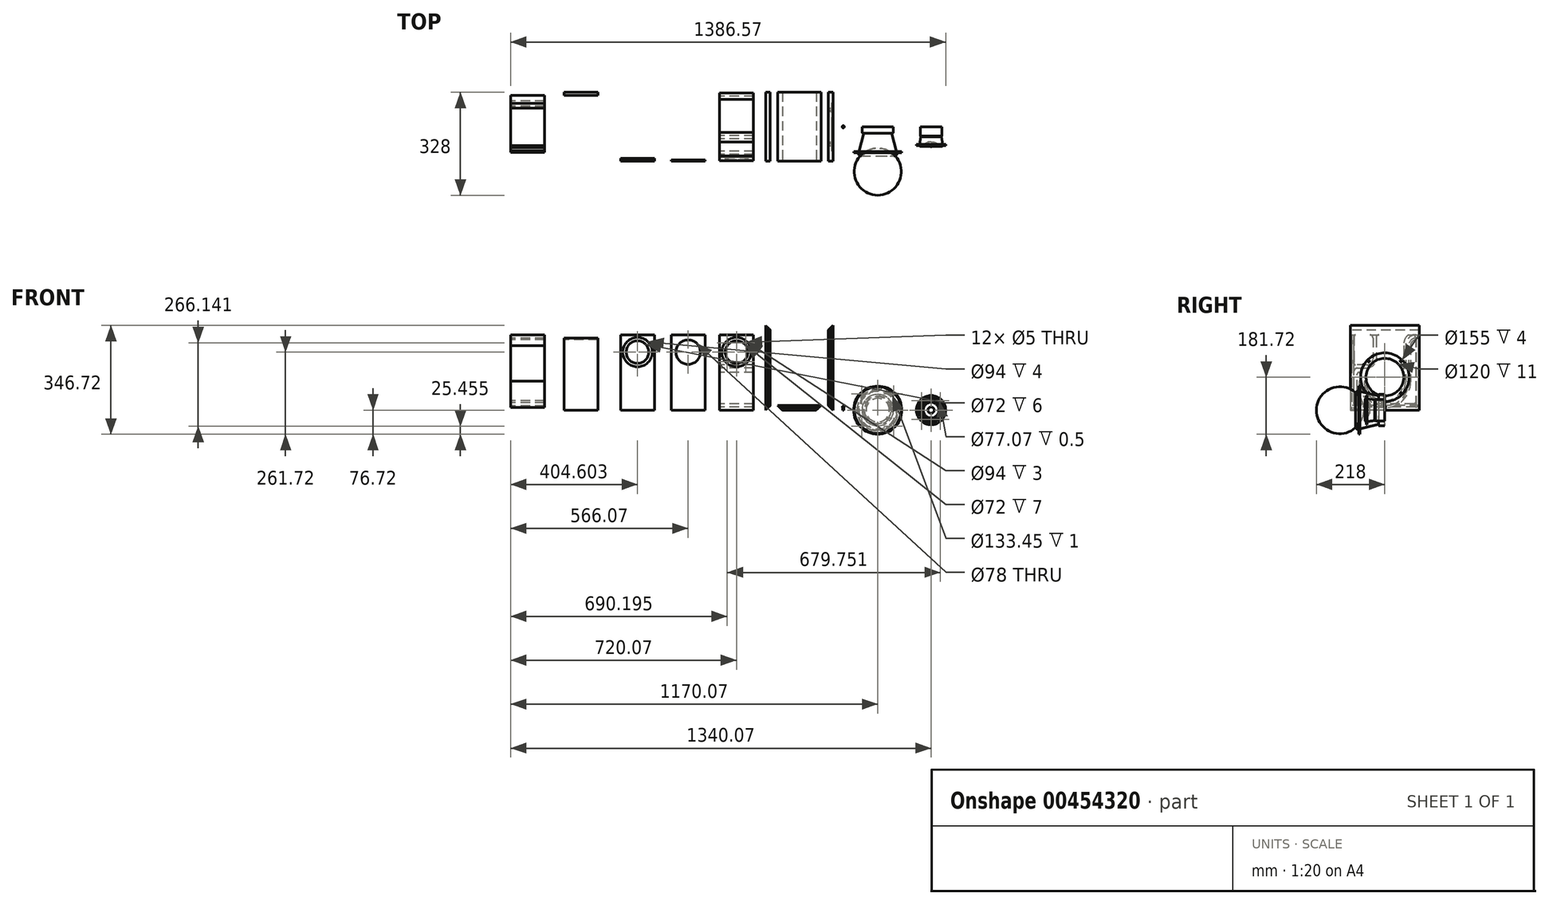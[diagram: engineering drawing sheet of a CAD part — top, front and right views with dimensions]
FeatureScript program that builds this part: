
annotation { "Feature Type Name" : "Feature", "Feature Type Description" : "" }
export const myFeature = defineFeature(function(context is Context, id is Id, definition is map)
    precondition{}
    {
        {
            var Q0;
            Q0=qCreatedBy(makeId("Top.planeOp"),FACE);
            var sketch = newSketch(context, id + "F0", { "sketchPlane" : qUnion([Q0])});
            skLineSegment(sketch, "E0", {"start": v(0, 207.9) * mm, "end": v(0, 427.9) * mm});
            skLineSegment(sketch, "E1", {"start": v(0, 427.9) * mm, "end": v(108, 427.9) * mm});
            skSolve(sketch);
        }
        {
            var Q0;
            Q0=qCreatedBy(makeId("Top.planeOp"),FACE);
            var sketch = newSketch(context, id + "F1", { "sketchPlane" : qUnion([Q0])});
            skLineSegment(sketch, "E2.bottom", {"start": v(-69, -110) * mm, "end": v(69, -110) * mm});
            skLineSegment(sketch, "E2.top", {"start": v(-69, 110) * mm, "end": v(69, 110) * mm});
            skLineSegment(sketch, "E2.left", {"start": v(-69, -110) * mm, "end": v(-69, 110) * mm});
            skLineSegment(sketch, "E2.right", {"start": v(69, -110) * mm, "end": v(69, 110) * mm});
            skPoint(sketch, "E2.middle", {"position": v(0, 0) * mm});
            skSolve(sketch);
        }
        {
            var Q0;
            Q0 = qSketchRegion(id + "F1", true);
            extrude(context, id + "F2", {"entities" : qUnion([Q0]), "depth" : 15 * mm});
        }
        {
            var Q0;
            Q0=makeQuery(id+"F2.opExtrude","SWEPT_FACE",FACE,{"disambiguationData":[OSD([sQuery(id+"F1.wireOp",EDGE,"E2.bottom")])]});
            var sketch = newSketch(context, id + "F3", { "sketchPlane" : qUnion([Q0])});
            skLineSegment(sketch, "E3.bottom", {"start": v(-69, 1) * mm, "end": v(69, 1) * mm});
            skLineSegment(sketch, "E3.top", {"start": v(-69, 2) * mm, "end": v(69, 2) * mm});
            skLineSegment(sketch, "E3.left", {"start": v(-69, 1) * mm, "end": v(-69, 2) * mm});
            skLineSegment(sketch, "E3.right", {"start": v(69, 1) * mm, "end": v(69, 2) * mm});
            skLineSegment(sketch, "E4.0.1.0", {"start": v(-69, 4) * mm, "end": v(69, 4) * mm});
            skLineSegment(sketch, "E4.0.1.1", {"start": v(-69, 3) * mm, "end": v(-69, 4) * mm});
            skLineSegment(sketch, "E4.0.1.2", {"start": v(-69, 3) * mm, "end": v(69, 3) * mm});
            skLineSegment(sketch, "E4.0.1.3", {"start": v(69, 3) * mm, "end": v(69, 4) * mm});
            skLineSegment(sketch, "E4.0.2.0", {"start": v(-69, 6) * mm, "end": v(69, 6) * mm});
            skLineSegment(sketch, "E4.0.2.1", {"start": v(-69, 5) * mm, "end": v(-69, 6) * mm});
            skLineSegment(sketch, "E4.0.2.2", {"start": v(-69, 5) * mm, "end": v(69, 5) * mm});
            skLineSegment(sketch, "E4.0.2.3", {"start": v(69, 5) * mm, "end": v(69, 6) * mm});
            skLineSegment(sketch, "E4.0.3.0", {"start": v(-69, 8) * mm, "end": v(69, 8) * mm});
            skLineSegment(sketch, "E4.0.3.1", {"start": v(-69, 7) * mm, "end": v(-69, 8) * mm});
            skLineSegment(sketch, "E4.0.3.2", {"start": v(-69, 7) * mm, "end": v(69, 7) * mm});
            skLineSegment(sketch, "E4.0.3.3", {"start": v(69, 7) * mm, "end": v(69, 8) * mm});
            skLineSegment(sketch, "E4.0.4.0", {"start": v(-69, 10) * mm, "end": v(69, 10) * mm});
            skLineSegment(sketch, "E4.0.4.1", {"start": v(-69, 9) * mm, "end": v(-69, 10) * mm});
            skLineSegment(sketch, "E4.0.4.2", {"start": v(-69, 9) * mm, "end": v(69, 9) * mm});
            skLineSegment(sketch, "E4.0.4.3", {"start": v(69, 9) * mm, "end": v(69, 10) * mm});
            skLineSegment(sketch, "E4.direction1", {"start": v(-69, 2) * mm, "end": v(-45, 2) * mm, "construction": true});
            skLineSegment(sketch, "E4.direction2", {"start": v(-69, 2) * mm, "end": v(-69, 4) * mm, "construction": true});
            skLineSegment(sketch, "E5.0.0.5", {"start": v(-69, 12) * mm, "end": v(69, 12) * mm});
            skLineSegment(sketch, "E5.3.0.5", {"start": v(-69, 11) * mm, "end": v(-69, 12) * mm});
            skLineSegment(sketch, "E5.6.0.5", {"start": v(-69, 11) * mm, "end": v(69, 11) * mm});
            skLineSegment(sketch, "E5.9.0.5", {"start": v(69, 11) * mm, "end": v(69, 12) * mm});
            skLineSegment(sketch, "E5.0.0.6", {"start": v(-69, 14) * mm, "end": v(69, 14) * mm});
            skLineSegment(sketch, "E5.3.0.6", {"start": v(-69, 13) * mm, "end": v(-69, 14) * mm});
            skLineSegment(sketch, "E5.6.0.6", {"start": v(-69, 13) * mm, "end": v(69, 13) * mm});
            skLineSegment(sketch, "E5.9.0.6", {"start": v(69, 13) * mm, "end": v(69, 14) * mm});
            skSolve(sketch);
        }
        {
            var Q0;
            Q0 = qSketchRegion(id + "F3", true);
            extrude(context, id + "F4", {"entities" : qUnion([Q0]), "operationType" : NewBodyOperationType.REMOVE, "oppositeDirection" : true, "depth" : 0.1 * mm});
        }
        {
            var Q0;
            Q0=makeQuery(id+"F2.opExtrude","SWEPT_FACE",FACE,{"disambiguationData":[OSD([sQuery(id+"F1.wireOp",EDGE,"E2.top")])]});
            var sketch = newSketch(context, id + "F5", { "sketchPlane" : qUnion([Q0])});
            skLineSegment(sketch, "E6.bottom", {"start": v(-75, 1) * mm, "end": v(75, 1) * mm});
            skLineSegment(sketch, "E6.top", {"start": v(-75, 2) * mm, "end": v(75, 2) * mm});
            skLineSegment(sketch, "E6.left", {"start": v(-75, 1) * mm, "end": v(-75, 2) * mm});
            skLineSegment(sketch, "E6.right", {"start": v(75, 1) * mm, "end": v(75, 2) * mm});
            skLineSegment(sketch, "E7.0.1.0", {"start": v(-75, 4) * mm, "end": v(75, 4) * mm});
            skLineSegment(sketch, "E7.0.1.1", {"start": v(-75, 3) * mm, "end": v(-75, 4) * mm});
            skLineSegment(sketch, "E7.0.1.2", {"start": v(-75, 3) * mm, "end": v(75, 3) * mm});
            skLineSegment(sketch, "E7.0.1.3", {"start": v(75, 3) * mm, "end": v(75, 4) * mm});
            skLineSegment(sketch, "E7.0.2.0", {"start": v(-75, 6) * mm, "end": v(75, 6) * mm});
            skLineSegment(sketch, "E7.0.2.1", {"start": v(-75, 5) * mm, "end": v(-75, 6) * mm});
            skLineSegment(sketch, "E7.0.2.2", {"start": v(-75, 5) * mm, "end": v(75, 5) * mm});
            skLineSegment(sketch, "E7.0.2.3", {"start": v(75, 5) * mm, "end": v(75, 6) * mm});
            skLineSegment(sketch, "E7.0.3.0", {"start": v(-75, 8) * mm, "end": v(75, 8) * mm});
            skLineSegment(sketch, "E7.0.3.1", {"start": v(-75, 7) * mm, "end": v(-75, 8) * mm});
            skLineSegment(sketch, "E7.0.3.2", {"start": v(-75, 7) * mm, "end": v(75, 7) * mm});
            skLineSegment(sketch, "E7.0.3.3", {"start": v(75, 7) * mm, "end": v(75, 8) * mm});
            skLineSegment(sketch, "E7.0.4.0", {"start": v(-75, 10) * mm, "end": v(75, 10) * mm});
            skLineSegment(sketch, "E7.0.4.1", {"start": v(-75, 9) * mm, "end": v(-75, 10) * mm});
            skLineSegment(sketch, "E7.0.4.2", {"start": v(-75, 9) * mm, "end": v(75, 9) * mm});
            skLineSegment(sketch, "E7.0.4.3", {"start": v(75, 9) * mm, "end": v(75, 10) * mm});
            skLineSegment(sketch, "E7.direction1", {"start": v(-75, 2) * mm, "end": v(-45, 2) * mm, "construction": true});
            skLineSegment(sketch, "E7.direction2", {"start": v(-75, 2) * mm, "end": v(-75, 4) * mm, "construction": true});
            skLineSegment(sketch, "E8.0.0.5", {"start": v(-75, 12) * mm, "end": v(75, 12) * mm});
            skLineSegment(sketch, "E8.3.0.5", {"start": v(-75, 11) * mm, "end": v(-75, 12) * mm});
            skLineSegment(sketch, "E8.6.0.5", {"start": v(-75, 11) * mm, "end": v(75, 11) * mm});
            skLineSegment(sketch, "E8.9.0.5", {"start": v(75, 11) * mm, "end": v(75, 12) * mm});
            skLineSegment(sketch, "E8.0.0.6", {"start": v(-75, 14) * mm, "end": v(75, 14) * mm});
            skLineSegment(sketch, "E8.3.0.6", {"start": v(-75, 13) * mm, "end": v(-75, 14) * mm});
            skLineSegment(sketch, "E8.6.0.6", {"start": v(-75, 13) * mm, "end": v(75, 13) * mm});
            skLineSegment(sketch, "E8.9.0.6", {"start": v(75, 13) * mm, "end": v(75, 14) * mm});
            skSolve(sketch);
        }
        {
            var Q0;
            Q0 = qSketchRegion(id + "F5", true);
            extrude(context, id + "F6", {"entities" : qUnion([Q0]), "operationType" : NewBodyOperationType.REMOVE, "oppositeDirection" : true, "depth" : 0.1 * mm});
        }
        {
            var Q0;
            {var subQ2=sQuery(id+"F1.wireOp",EDGE,"E2.bottom");Q0=makeQuery(id+"F4.boolean.opBoolean","SPLIT",FACE,{"disambiguationData":[TD([makeQuery(id+"F4.opExtrude","SWEPT_FACE",FACE,{"disambiguationData":[OSD([sQuery(id+"F3.wireOp",EDGE,"E3.bottom")])]})])],"derivedFrom":makeQuery(id+"F2.opExtrude","SWEPT_FACE",FACE,{"disambiguationData":[OSD([subQ2])]})});}
            var sketch = newSketch(context, id + "F7", { "sketchPlane" : qUnion([Q0])});
            skLineSegment(sketch, "E9", {"start": v(-69, 0) * mm, "end": v(-69, 15) * mm});
            skLineSegment(sketch, "E10", {"start": v(-69, 15) * mm, "end": v(-54, 0) * mm});
            skLineSegment(sketch, "E11", {"start": v(-54, 0) * mm, "end": v(-69, 0) * mm});
            skLineSegment(sketch, "E12", {"start": v(69, 0) * mm, "end": v(69, 15) * mm});
            skLineSegment(sketch, "E13", {"start": v(69, 15) * mm, "end": v(54, 0) * mm});
            skLineSegment(sketch, "E14", {"start": v(54, 0) * mm, "end": v(69, 0) * mm});
            skSolve(sketch);
        }
        {
            var Q0;
            Q0 = qSketchRegion(id + "F7", true);
            extrude(context, id + "F8", {"entities" : qUnion([Q0]), "operationType" : NewBodyOperationType.REMOVE, "oppositeDirection" : true, "depth" : 260 * mm});
        }
        {
            var Q0;
            Q0=qCreatedBy(makeId("Top.planeOp"),FACE);
            var sketch = newSketch(context, id + "F9", { "sketchPlane" : qUnion([Q0])});
            skLineSegment(sketch, "E15.bottom", {"start": v(-107.5, -110) * mm, "end": v(-92.5, -110) * mm});
            skLineSegment(sketch, "E15.top", {"start": v(-107.5, 110) * mm, "end": v(-92.5, 110) * mm});
            skLineSegment(sketch, "E15.left", {"start": v(-107.5, -110) * mm, "end": v(-107.5, 110) * mm});
            skLineSegment(sketch, "E15.right", {"start": v(-92.5, -110) * mm, "end": v(-92.5, 110) * mm});
            skPoint(sketch, "E15.middle", {"position": v(-100, 0) * mm});
            skSolve(sketch);
        }
        {
            var Q0;
            Q0 = qSketchRegion(id + "F9", true);
            extrude(context, id + "F10", {"entities" : qUnion([Q0]), "depth" : 270 * mm});
        }
        {
            var Q0;
            Q0=makeQuery(id+"F10.opExtrude","SWEPT_FACE",FACE,{"disambiguationData":[OSD([sQuery(id+"F9.wireOp",EDGE,"E15.bottom")])]});
            var sketch = newSketch(context, id + "F11", { "sketchPlane" : qUnion([Q0])});
            skLineSegment(sketch, "E16.bottom", {"start": v(-106.5, 270) * mm, "end": v(-105.5, 270) * mm});
            skLineSegment(sketch, "E16.top", {"start": v(-106.5, 0) * mm, "end": v(-105.5, 0) * mm});
            skLineSegment(sketch, "E16.left", {"start": v(-106.5, 270) * mm, "end": v(-106.5, 0) * mm});
            skLineSegment(sketch, "E16.right", {"start": v(-105.5, 270) * mm, "end": v(-105.5, 0) * mm});
            skLineSegment(sketch, "E17.1.0.0", {"start": v(-104.5, 270) * mm, "end": v(-103.5, 270) * mm});
            skLineSegment(sketch, "E17.1.0.1", {"start": v(-104.5, 270) * mm, "end": v(-104.5, 0) * mm});
            skLineSegment(sketch, "E17.1.0.2", {"start": v(-103.5, 270) * mm, "end": v(-103.5, 0) * mm});
            skLineSegment(sketch, "E17.1.0.3", {"start": v(-104.5, 0) * mm, "end": v(-103.5, 0) * mm});
            skLineSegment(sketch, "E17.2.0.0", {"start": v(-102.5, 270) * mm, "end": v(-101.5, 270) * mm});
            skLineSegment(sketch, "E17.2.0.1", {"start": v(-102.5, 270) * mm, "end": v(-102.5, 0) * mm});
            skLineSegment(sketch, "E17.2.0.2", {"start": v(-101.5, 270) * mm, "end": v(-101.5, 0) * mm});
            skLineSegment(sketch, "E17.2.0.3", {"start": v(-102.5, 0) * mm, "end": v(-101.5, 0) * mm});
            skLineSegment(sketch, "E17.3.0.0", {"start": v(-100.5, 270) * mm, "end": v(-99.5, 270) * mm});
            skLineSegment(sketch, "E17.3.0.1", {"start": v(-100.5, 270) * mm, "end": v(-100.5, 0) * mm});
            skLineSegment(sketch, "E17.3.0.2", {"start": v(-99.5, 270) * mm, "end": v(-99.5, 0) * mm});
            skLineSegment(sketch, "E17.3.0.3", {"start": v(-100.5, 0) * mm, "end": v(-99.5, 0) * mm});
            skLineSegment(sketch, "E17.4.0.0", {"start": v(-98.5, 270) * mm, "end": v(-97.5, 270) * mm});
            skLineSegment(sketch, "E17.4.0.1", {"start": v(-98.5, 270) * mm, "end": v(-98.5, 0) * mm});
            skLineSegment(sketch, "E17.4.0.2", {"start": v(-97.5, 270) * mm, "end": v(-97.5, 0) * mm});
            skLineSegment(sketch, "E17.4.0.3", {"start": v(-98.5, 0) * mm, "end": v(-97.5, 0) * mm});
            skLineSegment(sketch, "E17.direction1", {"start": v(-106.5, 270) * mm, "end": v(-104.5, 270) * mm, "construction": true});
            skLineSegment(sketch, "E18.0.5.0", {"start": v(-96.5, 270) * mm, "end": v(-95.5, 270) * mm});
            skLineSegment(sketch, "E18.3.5.0", {"start": v(-96.5, 270) * mm, "end": v(-96.5, 0) * mm});
            skLineSegment(sketch, "E18.6.5.0", {"start": v(-95.5, 270) * mm, "end": v(-95.5, 0) * mm});
            skLineSegment(sketch, "E18.9.5.0", {"start": v(-96.5, 0) * mm, "end": v(-95.5, 0) * mm});
            skLineSegment(sketch, "E18.0.6.0", {"start": v(-94.5, 270) * mm, "end": v(-93.5, 270) * mm});
            skLineSegment(sketch, "E18.3.6.0", {"start": v(-94.5, 270) * mm, "end": v(-94.5, 0) * mm});
            skLineSegment(sketch, "E18.6.6.0", {"start": v(-93.5, 270) * mm, "end": v(-93.5, 0) * mm});
            skLineSegment(sketch, "E18.9.6.0", {"start": v(-94.5, 0) * mm, "end": v(-93.5, 0) * mm});
            skSolve(sketch);
        }
        {
            var Q0;
            Q0 = qSketchRegion(id + "F11", true);
            extrude(context, id + "F12", {"entities" : qUnion([Q0]), "operationType" : NewBodyOperationType.REMOVE, "oppositeDirection" : true, "depth" : 0.1 * mm});
        }
        {
            var Q0;
            {var subQ1=sQuery(id+"F9.wireOp",EDGE,"E15.left");var subQ3=sQuery(id+"F9.wireOp",EDGE,"E15.bottom");Q0=makeQuery(id+"F12.boolean.opBoolean","SPLIT",FACE,{"disambiguationData":[TD([makeQuery(id+"F10.opExtrude","SWEPT_FACE",FACE,{"disambiguationData":[OSD([subQ1])]})])],"derivedFrom":makeQuery(id+"F10.opExtrude","SWEPT_FACE",FACE,{"disambiguationData":[OSD([subQ3])]})});}
            var sketch = newSketch(context, id + "F13", { "sketchPlane" : qUnion([Q0])});
            skLineSegment(sketch, "E19", {"start": v(-107.5, 270) * mm, "end": v(-92.5, 270) * mm});
            skLineSegment(sketch, "E20", {"start": v(-92.5, 270) * mm, "end": v(-92.5, 255) * mm});
            skLineSegment(sketch, "E21", {"start": v(-92.5, 255) * mm, "end": v(-107.5, 270) * mm});
            skLineSegment(sketch, "E22", {"start": v(-107.5, 0) * mm, "end": v(-92.5, 0) * mm});
            skLineSegment(sketch, "E23", {"start": v(-92.5, 0) * mm, "end": v(-92.5, 15) * mm});
            skLineSegment(sketch, "E24", {"start": v(-92.5, 15) * mm, "end": v(-107.5, 0) * mm});
            skSolve(sketch);
        }
        {
            var Q0;
            Q0 = qSketchRegion(id + "F13", true);
            extrude(context, id + "F14", {"entities" : qUnion([Q0]), "operationType" : NewBodyOperationType.REMOVE, "oppositeDirection" : true, "depth" : 260 * mm});
        }
        {
            var Q0;
            Q0=makeQuery(id+"F10.opExtrude","SWEPT_FACE",FACE,{"disambiguationData":[OSD([sQuery(id+"F9.wireOp",EDGE,"E15.top")])]});
            var sketch = newSketch(context, id + "F15", { "sketchPlane" : qUnion([Q0])});
            skLineSegment(sketch, "E25.bottom", {"start": v(93.5, 275) * mm, "end": v(94.5, 275) * mm});
            skLineSegment(sketch, "E25.top", {"start": v(93.5, 0) * mm, "end": v(94.5, 0) * mm});
            skLineSegment(sketch, "E25.left", {"start": v(93.5, 275) * mm, "end": v(93.5, 0) * mm});
            skLineSegment(sketch, "E25.right", {"start": v(94.5, 275) * mm, "end": v(94.5, 0) * mm});
            skLineSegment(sketch, "E26.1.0.0", {"start": v(95.5, 275) * mm, "end": v(96.5, 275) * mm});
            skLineSegment(sketch, "E26.1.0.1", {"start": v(95.5, 275) * mm, "end": v(95.5, 0) * mm});
            skLineSegment(sketch, "E26.1.0.2", {"start": v(96.5, 275) * mm, "end": v(96.5, 0) * mm});
            skLineSegment(sketch, "E26.1.0.3", {"start": v(95.5, 0) * mm, "end": v(96.5, 0) * mm});
            skLineSegment(sketch, "E26.2.0.0", {"start": v(97.5, 275) * mm, "end": v(98.5, 275) * mm});
            skLineSegment(sketch, "E26.2.0.1", {"start": v(97.5, 275) * mm, "end": v(97.5, 0) * mm});
            skLineSegment(sketch, "E26.2.0.2", {"start": v(98.5, 275) * mm, "end": v(98.5, 0) * mm});
            skLineSegment(sketch, "E26.2.0.3", {"start": v(97.5, 0) * mm, "end": v(98.5, 0) * mm});
            skLineSegment(sketch, "E26.3.0.0", {"start": v(99.5, 275) * mm, "end": v(100.5, 275) * mm});
            skLineSegment(sketch, "E26.3.0.1", {"start": v(99.5, 275) * mm, "end": v(99.5, 0) * mm});
            skLineSegment(sketch, "E26.3.0.2", {"start": v(100.5, 275) * mm, "end": v(100.5, 0) * mm});
            skLineSegment(sketch, "E26.3.0.3", {"start": v(99.5, 0) * mm, "end": v(100.5, 0) * mm});
            skLineSegment(sketch, "E26.4.0.0", {"start": v(101.5, 275) * mm, "end": v(102.5, 275) * mm});
            skLineSegment(sketch, "E26.4.0.1", {"start": v(101.5, 275) * mm, "end": v(101.5, 0) * mm});
            skLineSegment(sketch, "E26.4.0.2", {"start": v(102.5, 275) * mm, "end": v(102.5, 0) * mm});
            skLineSegment(sketch, "E26.4.0.3", {"start": v(101.5, 0) * mm, "end": v(102.5, 0) * mm});
            skLineSegment(sketch, "E26.direction1", {"start": v(93.5, 275) * mm, "end": v(95.5, 275) * mm, "construction": true});
            skLineSegment(sketch, "E27.0.5.0", {"start": v(103.5, 275) * mm, "end": v(104.5, 275) * mm});
            skLineSegment(sketch, "E27.3.5.0", {"start": v(103.5, 275) * mm, "end": v(103.5, 0) * mm});
            skLineSegment(sketch, "E27.6.5.0", {"start": v(104.5, 275) * mm, "end": v(104.5, 0) * mm});
            skLineSegment(sketch, "E27.9.5.0", {"start": v(103.5, 0) * mm, "end": v(104.5, 0) * mm});
            skLineSegment(sketch, "E27.0.6.0", {"start": v(105.5, 275) * mm, "end": v(106.5, 275) * mm});
            skLineSegment(sketch, "E27.3.6.0", {"start": v(105.5, 275) * mm, "end": v(105.5, 0) * mm});
            skLineSegment(sketch, "E27.6.6.0", {"start": v(106.5, 275) * mm, "end": v(106.5, 0) * mm});
            skLineSegment(sketch, "E27.9.6.0", {"start": v(105.5, 0) * mm, "end": v(106.5, 0) * mm});
            skSolve(sketch);
        }
        {
            var Q0;
            Q0 = qSketchRegion(id + "F15", true);
            extrude(context, id + "F16", {"entities" : qUnion([Q0]), "operationType" : NewBodyOperationType.REMOVE, "oppositeDirection" : true, "depth" : 0.1 * mm});
        }
        {
            var Q0;
            Q0=qCreatedBy(makeId("Top.planeOp"),FACE);
            var sketch = newSketch(context, id + "F17", { "sketchPlane" : qUnion([Q0])});
            skLineSegment(sketch, "E28.bottom", {"start": v(92.5, 110) * mm, "end": v(107.5, 110) * mm});
            skLineSegment(sketch, "E28.top", {"start": v(92.5, -110) * mm, "end": v(107.5, -110) * mm});
            skLineSegment(sketch, "E28.left", {"start": v(92.5, 110) * mm, "end": v(92.5, -110) * mm});
            skLineSegment(sketch, "E28.right", {"start": v(107.5, 110) * mm, "end": v(107.5, -110) * mm});
            skPoint(sketch, "E28.middle", {"position": v(100, 0) * mm});
            skSolve(sketch);
        }
        {
            var Q0;
            Q0 = qSketchRegion(id + "F17", true);
            extrude(context, id + "F18", {"entities" : qUnion([Q0]), "depth" : 270 * mm});
        }
        {
            var Q0;
            Q0=makeQuery(id+"F18.opExtrude","SWEPT_FACE",FACE,{"disambiguationData":[OSD([sQuery(id+"F17.wireOp",EDGE,"E28.top")])]});
            var sketch = newSketch(context, id + "F19", { "sketchPlane" : qUnion([Q0])});
            skLineSegment(sketch, "E29.bottom", {"start": v(93.5, 280) * mm, "end": v(94.5, 280) * mm});
            skLineSegment(sketch, "E29.top", {"start": v(93.5, 0) * mm, "end": v(94.5, 0) * mm});
            skLineSegment(sketch, "E29.left", {"start": v(93.5, 280) * mm, "end": v(93.5, 0) * mm});
            skLineSegment(sketch, "E29.right", {"start": v(94.5, 280) * mm, "end": v(94.5, 0) * mm});
            skLineSegment(sketch, "E30.1.0.0", {"start": v(95.5, 280) * mm, "end": v(95.5, 0) * mm});
            skLineSegment(sketch, "E30.1.0.1", {"start": v(95.5, 280) * mm, "end": v(96.5, 280) * mm});
            skLineSegment(sketch, "E30.1.0.2", {"start": v(96.5, 280) * mm, "end": v(96.5, 0) * mm});
            skLineSegment(sketch, "E30.1.0.3", {"start": v(95.5, 0) * mm, "end": v(96.5, 0) * mm});
            skLineSegment(sketch, "E30.2.0.0", {"start": v(97.5, 280) * mm, "end": v(97.5, 0) * mm});
            skLineSegment(sketch, "E30.2.0.1", {"start": v(97.5, 280) * mm, "end": v(98.5, 280) * mm});
            skLineSegment(sketch, "E30.2.0.2", {"start": v(98.5, 280) * mm, "end": v(98.5, 0) * mm});
            skLineSegment(sketch, "E30.2.0.3", {"start": v(97.5, 0) * mm, "end": v(98.5, 0) * mm});
            skLineSegment(sketch, "E30.3.0.0", {"start": v(99.5, 280) * mm, "end": v(99.5, 0) * mm});
            skLineSegment(sketch, "E30.3.0.1", {"start": v(99.5, 280) * mm, "end": v(100.5, 280) * mm});
            skLineSegment(sketch, "E30.3.0.2", {"start": v(100.5, 280) * mm, "end": v(100.5, 0) * mm});
            skLineSegment(sketch, "E30.3.0.3", {"start": v(99.5, 0) * mm, "end": v(100.5, 0) * mm});
            skLineSegment(sketch, "E30.4.0.0", {"start": v(101.5, 280) * mm, "end": v(101.5, 0) * mm});
            skLineSegment(sketch, "E30.4.0.1", {"start": v(101.5, 280) * mm, "end": v(102.5, 280) * mm});
            skLineSegment(sketch, "E30.4.0.2", {"start": v(102.5, 280) * mm, "end": v(102.5, 0) * mm});
            skLineSegment(sketch, "E30.4.0.3", {"start": v(101.5, 0) * mm, "end": v(102.5, 0) * mm});
            skLineSegment(sketch, "E30.5.0.0", {"start": v(103.5, 280) * mm, "end": v(103.5, 0) * mm});
            skLineSegment(sketch, "E30.5.0.1", {"start": v(103.5, 280) * mm, "end": v(104.5, 280) * mm});
            skLineSegment(sketch, "E30.5.0.2", {"start": v(104.5, 280) * mm, "end": v(104.5, 0) * mm});
            skLineSegment(sketch, "E30.5.0.3", {"start": v(103.5, 0) * mm, "end": v(104.5, 0) * mm});
            skLineSegment(sketch, "E30.6.0.0", {"start": v(105.5, 280) * mm, "end": v(105.5, 0) * mm});
            skLineSegment(sketch, "E30.6.0.1", {"start": v(105.5, 280) * mm, "end": v(106.5, 280) * mm});
            skLineSegment(sketch, "E30.6.0.2", {"start": v(106.5, 280) * mm, "end": v(106.5, 0) * mm});
            skLineSegment(sketch, "E30.6.0.3", {"start": v(105.5, 0) * mm, "end": v(106.5, 0) * mm});
            skLineSegment(sketch, "E30.direction1", {"start": v(93.5, 0) * mm, "end": v(95.5, 0) * mm, "construction": true});
            skSolve(sketch);
        }
        {
            var Q0;
            Q0 = qSketchRegion(id + "F19", true);
            extrude(context, id + "F20", {"entities" : qUnion([Q0]), "operationType" : NewBodyOperationType.REMOVE, "oppositeDirection" : true, "depth" : 0.1 * mm});
        }
        {
            var Q0;
            {var subQ0=sQuery(id+"F17.wireOp",EDGE,"E28.right");var subQ2=sQuery(id+"F17.wireOp",EDGE,"E28.top");Q0=makeQuery(id+"F20.boolean.opBoolean","SPLIT",FACE,{"disambiguationData":[TD([makeQuery(id+"F18.opExtrude","SWEPT_FACE",FACE,{"disambiguationData":[OSD([subQ0])]})])],"derivedFrom":makeQuery(id+"F18.opExtrude","SWEPT_FACE",FACE,{"disambiguationData":[OSD([subQ2])]})});}
            var sketch = newSketch(context, id + "F21", { "sketchPlane" : qUnion([Q0])});
            skLineSegment(sketch, "E31", {"start": v(107.5, 270) * mm, "end": v(92.5, 270) * mm});
            skLineSegment(sketch, "E32", {"start": v(92.5, 270) * mm, "end": v(92.5, 255) * mm});
            skLineSegment(sketch, "E33", {"start": v(92.5, 255) * mm, "end": v(107.5, 270) * mm});
            skLineSegment(sketch, "E34", {"start": v(107.5, 0) * mm, "end": v(92.5, 0) * mm});
            skLineSegment(sketch, "E35", {"start": v(92.5, 0) * mm, "end": v(92.5, 15) * mm});
            skLineSegment(sketch, "E36", {"start": v(92.5, 15) * mm, "end": v(107.5, 0) * mm});
            skSolve(sketch);
        }
        {
            var Q0;
            Q0 = qSketchRegion(id + "F21", true);
            extrude(context, id + "F22", {"entities" : qUnion([Q0]), "operationType" : NewBodyOperationType.REMOVE, "oppositeDirection" : true, "depth" : 260 * mm});
        }
        {
            var Q0;
            Q0=makeQuery(id+"F18.opExtrude","SWEPT_FACE",FACE,{"disambiguationData":[OSD([sQuery(id+"F17.wireOp",EDGE,"E28.bottom")])]});
            var sketch = newSketch(context, id + "F23", { "sketchPlane" : qUnion([Q0])});
            skLineSegment(sketch, "E37.bottom", {"start": v(-106.5, 275) * mm, "end": v(-105.5, 275) * mm});
            skLineSegment(sketch, "E37.top", {"start": v(-106.5, -6.67) * mm, "end": v(-105.5, -6.67) * mm});
            skLineSegment(sketch, "E37.left", {"start": v(-106.5, 275) * mm, "end": v(-106.5, -6.67) * mm});
            skLineSegment(sketch, "E37.right", {"start": v(-105.5, 275) * mm, "end": v(-105.5, -6.67) * mm});
            skLineSegment(sketch, "E38.1.0.0", {"start": v(-104.5, 275) * mm, "end": v(-103.5, 275) * mm});
            skLineSegment(sketch, "E38.1.0.1", {"start": v(-104.5, 275) * mm, "end": v(-104.5, -6.67) * mm});
            skLineSegment(sketch, "E38.1.0.2", {"start": v(-103.5, 275) * mm, "end": v(-103.5, -6.67) * mm});
            skLineSegment(sketch, "E38.1.0.3", {"start": v(-104.5, -6.67) * mm, "end": v(-103.5, -6.67) * mm});
            skLineSegment(sketch, "E38.2.0.0", {"start": v(-102.5, 275) * mm, "end": v(-101.5, 275) * mm});
            skLineSegment(sketch, "E38.2.0.1", {"start": v(-102.5, 275) * mm, "end": v(-102.5, -6.67) * mm});
            skLineSegment(sketch, "E38.2.0.2", {"start": v(-101.5, 275) * mm, "end": v(-101.5, -6.67) * mm});
            skLineSegment(sketch, "E38.2.0.3", {"start": v(-102.5, -6.67) * mm, "end": v(-101.5, -6.67) * mm});
            skLineSegment(sketch, "E38.3.0.0", {"start": v(-100.5, 275) * mm, "end": v(-99.5, 275) * mm});
            skLineSegment(sketch, "E38.3.0.1", {"start": v(-100.5, 275) * mm, "end": v(-100.5, -6.67) * mm});
            skLineSegment(sketch, "E38.3.0.2", {"start": v(-99.5, 275) * mm, "end": v(-99.5, -6.67) * mm});
            skLineSegment(sketch, "E38.3.0.3", {"start": v(-100.5, -6.67) * mm, "end": v(-99.5, -6.67) * mm});
            skLineSegment(sketch, "E38.4.0.0", {"start": v(-98.5, 275) * mm, "end": v(-97.5, 275) * mm});
            skLineSegment(sketch, "E38.4.0.1", {"start": v(-98.5, 275) * mm, "end": v(-98.5, -6.67) * mm});
            skLineSegment(sketch, "E38.4.0.2", {"start": v(-97.5, 275) * mm, "end": v(-97.5, -6.67) * mm});
            skLineSegment(sketch, "E38.4.0.3", {"start": v(-98.5, -6.67) * mm, "end": v(-97.5, -6.67) * mm});
            skLineSegment(sketch, "E38.direction1", {"start": v(-106.5, 275) * mm, "end": v(-104.5, 275) * mm, "construction": true});
            skLineSegment(sketch, "E39.0.5.0", {"start": v(-96.5, 275) * mm, "end": v(-95.5, 275) * mm});
            skLineSegment(sketch, "E39.3.5.0", {"start": v(-96.5, 275) * mm, "end": v(-96.5, -6.67) * mm});
            skLineSegment(sketch, "E39.6.5.0", {"start": v(-95.5, 275) * mm, "end": v(-95.5, -6.67) * mm});
            skLineSegment(sketch, "E39.9.5.0", {"start": v(-96.5, -6.67) * mm, "end": v(-95.5, -6.67) * mm});
            skLineSegment(sketch, "E39.0.6.0", {"start": v(-94.5, 275) * mm, "end": v(-93.5, 275) * mm});
            skLineSegment(sketch, "E39.3.6.0", {"start": v(-94.5, 275) * mm, "end": v(-94.5, -6.67) * mm});
            skLineSegment(sketch, "E39.6.6.0", {"start": v(-93.5, 275) * mm, "end": v(-93.5, -6.67) * mm});
            skLineSegment(sketch, "E39.9.6.0", {"start": v(-94.5, -6.67) * mm, "end": v(-93.5, -6.67) * mm});
            skSolve(sketch);
        }
        {
            var Q0;
            Q0 = qSketchRegion(id + "F23", true);
            extrude(context, id + "F24", {"entities" : qUnion([Q0]), "operationType" : NewBodyOperationType.REMOVE, "oppositeDirection" : true, "depth" : 0.1 * mm});
        }
        {
            var Q0;
            Q0=makeQuery(id+"F18.opExtrude","SWEPT_FACE",FACE,{"disambiguationData":[OSD([sQuery(id+"F17.wireOp",EDGE,"E28.right")])]});
            var sketch = newSketch(context, id + "F25", { "sketchPlane" : qUnion([Q0])});
            skCircle(sketch, "E40", {"center": v(0, 105) * mm, "radius": 77.5 * mm});
            skSolve(sketch);
        }
        {
            var Q0;
            Q0 = qSketchRegion(id + "F25", true);
            extrude(context, id + "F26", {"entities" : qUnion([Q0]), "operationType" : NewBodyOperationType.REMOVE, "oppositeDirection" : true, "depth" : 4 * mm});
        }
        {
            var Q0;
            Q0=makeQuery(id+"F26.boolean.opBoolean","COPY",FACE,{"derivedFrom":makeQuery(id+"F26.opExtrude","CAP_FACE",FACE,{"disambiguationData":[OSD([sQuery(id+"F25.wireOp",EDGE,"E40")])],"isStart":false})});
            var sketch = newSketch(context, id + "F27", { "sketchPlane" : qUnion([Q0])});
            skCircle(sketch, "E41", {"center": v(0, 105) * mm, "radius": 60 * mm});
            skSolve(sketch);
        }
        {
            var Q0;
            Q0 = qSketchRegion(id + "F27", true);
            extrude(context, id + "F28", {"entities" : qUnion([Q0]), "operationType" : NewBodyOperationType.REMOVE, "oppositeDirection" : true, "depth" : 11 * mm});
        }
        {
            var Q0;
            Q0=qCreatedBy(makeId("Top.planeOp"),FACE);
            var sketch = newSketch(context, id + "F29", { "sketchPlane" : qUnion([Q0])});
            skLineSegment(sketch, "E42.bottom", {"start": v(-254, -108) * mm, "end": v(-146, -108) * mm});
            skLineSegment(sketch, "E42.top", {"start": v(-254, 108) * mm, "end": v(-146, 108) * mm});
            skLineSegment(sketch, "E42.left", {"start": v(-254, -108) * mm, "end": v(-254, 108) * mm});
            skLineSegment(sketch, "E42.right", {"start": v(-146, -108) * mm, "end": v(-146, 108) * mm});
            skPoint(sketch, "E42.middle", {"position": v(-200, 0) * mm});
            skSolve(sketch);
        }
        {
            var Q0;
            Q0 = qSketchRegion(id + "F29", true);
            extrude(context, id + "F30", {"entities" : qUnion([Q0]), "depth" : 240 * mm});
        }
        {
            var Q0;
            Q0=makeQuery(id+"F30.opExtrude","SWEPT_FACE",FACE,{"disambiguationData":[OSD([sQuery(id+"F29.wireOp",EDGE,"E42.left")])]});
            var sketch = newSketch(context, id + "F31", { "sketchPlane" : qUnion([Q0])});
            skArc(sketch, "E43", {"start": v(78, 0) * mm, "mid": v(92.14, 5.86) * mm, "end": v(98, 20) * mm});
            skLineSegment(sketch, "E44", {"start": v(-98, 230) * mm, "end": v(-98, 25) * mm});
            skLineSegment(sketch, "E45", {"start": v(-98, 10) * mm, "end": v(78, 10) * mm});
            skLineSegment(sketch, "E46", {"start": v(98, 20) * mm, "end": v(98, 124) * mm});
            skLineSegment(sketch, "E47", {"start": v(78, 0) * mm, "end": v(-108, 0) * mm});
            skArc(sketch, "E48", {"start": v(98, 124) * mm, "mid": v(95.07, 131.07) * mm, "end": v(88, 134) * mm});
            skLineSegment(sketch, "E49", {"start": v(88, 134) * mm, "end": v(88, 134) * mm});
            skArc(sketch, "E50", {"start": v(-98, 25) * mm, "mid": v(-96.54, 21.46) * mm, "end": v(-93, 20) * mm});
            skLineSegment(sketch, "E51", {"start": v(-88, 240) * mm, "end": v(18, 240) * mm});
            skArc(sketch, "E52", {"start": v(-108, 20) * mm, "mid": v(-105.07, 12.93) * mm, "end": v(-98, 10) * mm});
            skArc(sketch, "E53", {"start": v(-88, 240) * mm, "mid": v(-95.07, 237.07) * mm, "end": v(-98, 230) * mm});
            skArc(sketch, "E54", {"start": v(28, 230) * mm, "mid": v(25.07, 237.07) * mm, "end": v(18, 240) * mm});
            skLineSegment(sketch, "E55", {"start": v(-108, 20) * mm, "end": v(-108, 0) * mm});
            skLineSegment(sketch, "E56", {"start": v(88, 134) * mm, "end": v(58, 134) * mm});
            skLineSegment(sketch, "E57", {"start": v(48, 240) * mm, "end": v(93, 240) * mm});
            skArc(sketch, "E58", {"start": v(48, 240) * mm, "mid": v(40.93, 237.07) * mm, "end": v(38, 230) * mm});
            skArc(sketch, "E59", {"start": v(38, 164) * mm, "mid": v(43.86, 149.86) * mm, "end": v(58, 144) * mm});
            skArc(sketch, "E60", {"start": v(28, 164) * mm, "mid": v(36.79, 142.79) * mm, "end": v(58, 134) * mm});
            skLineSegment(sketch, "E61", {"start": v(28, 230) * mm, "end": v(28, 164) * mm});
            skLineSegment(sketch, "E62", {"start": v(38, 230) * mm, "end": v(38, 164) * mm});
            skArc(sketch, "E63", {"start": v(78, 10) * mm, "mid": v(85.07, 12.93) * mm, "end": v(88, 20) * mm});
            skLineSegment(sketch, "E64", {"start": v(88, 20) * mm, "end": v(88, 115) * mm});
            skLineSegment(sketch, "E65", {"start": v(58, 144) * mm, "end": v(93, 144) * mm});
            skArc(sketch, "E66", {"start": v(93, 144) * mm, "mid": v(96.54, 145.46) * mm, "end": v(98, 149) * mm});
            skArc(sketch, "E67", {"start": v(98, 235) * mm, "mid": v(96.54, 238.54) * mm, "end": v(93, 240) * mm});
            skLineSegment(sketch, "E68", {"start": v(98, 235) * mm, "end": v(98, 149) * mm});
            skLineSegment(sketch, "E69", {"start": v(-93, 20) * mm, "end": v(73, 20) * mm});
            skArc(sketch, "E70", {"start": v(73, 20) * mm, "mid": v(76.54, 21.46) * mm, "end": v(78, 25) * mm});
            skLineSegment(sketch, "E71", {"start": v(78, 25) * mm, "end": v(78, 115) * mm});
            skArc(sketch, "E72", {"start": v(88, 115) * mm, "mid": v(83, 120) * mm, "end": v(78, 115) * mm});
            skSolve(sketch);
        }
        {
            var Q0;
            Q0 = qSketchRegion(id + "F31", true);
            extrude(context, id + "F32", {"entities" : qUnion([Q0]), "operationType" : NewBodyOperationType.REMOVE, "oppositeDirection" : true, "depth" : 120 * mm});
        }
        {
            var Q0;
            Q0=makeQuery(id+"F30.opExtrude","SWEPT_FACE",FACE,{"disambiguationData":[OSD([sQuery(id+"F29.wireOp",EDGE,"E42.bottom")])]});
            var sketch = newSketch(context, id + "F33", { "sketchPlane" : qUnion([Q0])});
            skPoint(sketch, "E73.centerSnap0", {"position": v(-200, 240) * mm});
            skCircle(sketch, "E74", {"center": v(-200, 185) * mm, "radius": 47 * mm});
            skSolve(sketch);
        }
        {
            var Q0;
            Q0 = qSketchRegion(id + "F33", true);
            extrude(context, id + "F34", {"entities" : qUnion([Q0]), "operationType" : NewBodyOperationType.REMOVE, "oppositeDirection" : true, "depth" : 3 * mm});
        }
        {
            var Q0;
            Q0=makeQuery(id+"F30.opExtrude","SWEPT_FACE",FACE,{"disambiguationData":[OSD([sQuery(id+"F29.wireOp",EDGE,"E42.bottom")])]});
            var sketch = newSketch(context, id + "F35", { "sketchPlane" : qUnion([Q0])});
            skPoint(sketch, "E75.centerSnap0", {"position": v(-200, 240) * mm});
            skCircle(sketch, "E76", {"center": v(-200, 185) * mm, "radius": 36 * mm});
            skSolve(sketch);
        }
        {
            var Q0;
            Q0 = qSketchRegion(id + "F35", true);
            extrude(context, id + "F36", {"entities" : qUnion([Q0]), "operationType" : NewBodyOperationType.REMOVE, "oppositeDirection" : true, "depth" : 20 * mm});
        }
        {
            var Q0;
            Q0=qCreatedBy(makeId("Front.planeOp"),FACE);
            var sketch = newSketch(context, id + "F37", { "sketchPlane" : qUnion([Q0])});
            skCircle(sketch, "E77", {"center": v(250, 0) * mm, "radius": 77.5 * mm});
            skSolve(sketch);
        }
        {
            var Q0;
            Q0 = qSketchRegion(id + "F37", true);
            extrude(context, id + "F38", {"entities" : qUnion([Q0]), "depth" : 93 * mm});
        }
        {
            var Q0;
            Q0=qCreatedBy(makeId("Top.planeOp"),FACE);
            var sketch = newSketch(context, id + "F39", { "sketchPlane" : qUnion([Q0])});
            skLineSegment(sketch, "E78", {"start": v(250, 30.76) * mm, "end": v(250, -119.24) * mm, "construction": true});
            skSolve(sketch);
        }
        {
            var Q0;
            Q0=qCreatedBy(makeId("Top.planeOp"),FACE);
            var sketch = newSketch(context, id + "F40", { "sketchPlane" : qUnion([Q0])});
            skArc(sketch, "E79", {"start": v(292.5, -83) * mm, "mid": v(302.5, -93) * mm, "end": v(312.5, -83) * mm});
            skArc(sketch, "E80", {"start": v(292.5, -83) * mm, "mid": v(290.46, -80.04) * mm, "end": v(287.5, -78) * mm});
            skArc(sketch, "E81", {"start": v(287.5, -78) * mm, "mid": v(269.4, -70.53) * mm, "end": v(250, -68) * mm});
            skLineSegment(sketch, "E82", {"start": v(250, -68) * mm, "end": v(250, -95) * mm});
            skLineSegment(sketch, "E83", {"start": v(250, -95) * mm, "end": v(332, -95) * mm});
            skLineSegment(sketch, "E84", {"start": v(250, 0) * mm, "end": v(300, 0) * mm});
            skLineSegment(sketch, "E85", {"start": v(300, 0) * mm, "end": v(300, -20) * mm});
            skLineSegment(sketch, "E86", {"start": v(300, -20) * mm, "end": v(295, -20) * mm});
            skLineSegment(sketch, "E87", {"start": v(295, -20) * mm, "end": v(310, -79.4) * mm});
            skLineSegment(sketch, "E88", {"start": v(332, -95) * mm, "end": v(332, 5) * mm});
            skLineSegment(sketch, "E89", {"start": v(332, 5) * mm, "end": v(250, 5) * mm});
            skLineSegment(sketch, "E90", {"start": v(250, 5) * mm, "end": v(250, 0) * mm});
            skLineSegment(sketch, "E91", {"start": v(310, -79.4) * mm, "end": v(326.72, -79.4) * mm});
            skLineSegment(sketch, "E92", {"start": v(326.72, -79.4) * mm, "end": v(326.72, -83) * mm});
            skLineSegment(sketch, "E93", {"start": v(326.72, -83) * mm, "end": v(316.72, -83) * mm});
            skLineSegment(sketch, "E94", {"start": v(316.72, -83) * mm, "end": v(316.72, -82) * mm});
            skLineSegment(sketch, "E95", {"start": v(316.72, -82) * mm, "end": v(315.72, -82) * mm});
            skLineSegment(sketch, "E96", {"start": v(315.72, -82) * mm, "end": v(315.72, -83) * mm});
            skLineSegment(sketch, "E97", {"start": v(315.72, -83) * mm, "end": v(312.5, -83) * mm});
            skSolve(sketch);
        }
        {
            var Q0;
            Q0 = qSketchRegion(id + "F40", true);
            var Q1;
            Q1=sQuery(id+"F39.wireOp",EDGE,"E78");
            revolve(context, id + "F41", {"operationType" : NewBodyOperationType.REMOVE, "entities" : qUnion([Q0]), "axis" : qUnion([Q1]), "revolveType" : RevolveType.FULL, "oppositeDirection" : true});
        }
        {
            var Q0;
            Q0=makeQuery(id+"F41.boolean.opBoolean","COPY",FACE,{"derivedFrom":makeQuery(id+"F41.opRevolve","SWEPT_FACE",FACE,{"disambiguationData":[OSD([sQuery(id+"F40.wireOp",EDGE,"E93")])]})});
            var sketch = newSketch(context, id + "F42", { "sketchPlane" : qUnion([Q0])});
            skPoint(sketch, "E98.middle", {"position": v(250, 0) * mm});
            skLineSegment(sketch, "E99.bottom", {"start": v(198.73, -51.27) * mm, "end": v(301.27, -51.27) * mm, "construction": true});
            skLineSegment(sketch, "E99.top", {"start": v(198.73, 51.27) * mm, "end": v(301.27, 51.27) * mm, "construction": true});
            skLineSegment(sketch, "E99.left", {"start": v(198.73, -51.27) * mm, "end": v(198.73, 51.27) * mm, "construction": true});
            skLineSegment(sketch, "E99.right", {"start": v(301.27, -51.27) * mm, "end": v(301.27, 51.27) * mm, "construction": true});
            skCircle(sketch, "E100", {"center": v(198.73, 51.27) * mm, "radius": 2.5 * mm});
            skCircle(sketch, "E101", {"center": v(301.27, 51.27) * mm, "radius": 2.5 * mm});
            skCircle(sketch, "E102", {"center": v(301.27, -51.27) * mm, "radius": 2.5 * mm});
            skCircle(sketch, "E103", {"center": v(198.73, -51.27) * mm, "radius": 2.5 * mm});
            skSolve(sketch);
        }
        {
            var Q0;
            Q0 = qSketchRegion(id + "F42", true);
            extrude(context, id + "F43", {"entities" : qUnion([Q0]), "operationType" : NewBodyOperationType.REMOVE, "oppositeDirection" : true, "depth" : 5 * mm});
        }
        {
            var Q0;
            Q0=makeQuery(id+"F41.boolean.opBoolean","COPY",EDGE,{"derivedFrom":makeQuery(id+"F41.opRevolve","SWEPT_EDGE",EDGE,{"disambiguationData":[OSD([sQuery(id+"F40.wireOp",EDGE,"E84"),sQuery(id+"F40.wireOp",EDGE,"E85")])]})});
            var Q1;
            Q1=makeQuery(id+"F41.boolean.opBoolean","COPY",EDGE,{"derivedFrom":makeQuery(id+"F41.opRevolve","SWEPT_EDGE",EDGE,{"disambiguationData":[OSD([sQuery(id+"F40.wireOp",EDGE,"E85"),sQuery(id+"F40.wireOp",EDGE,"E86")])]})});
            fillet(context, id + "F44", {"entities" : qUnion([Q0, Q1]), "radius" : 2 * mm, "tangentPropagation" : true, "allowEdgeOverflow" : false});
        }
        {
            var Q0;
            Q0=qCreatedBy(makeId("Front.planeOp"),FACE);
            var sketch = newSketch(context, id + "F45", { "sketchPlane" : qUnion([Q0])});
            skCircle(sketch, "E104", {"center": v(420, 0) * mm, "radius": 46.5 * mm});
            skSolve(sketch);
        }
        {
            var Q0;
            Q0 = qSketchRegion(id + "F45", true);
            extrude(context, id + "F46", {"entities" : qUnion([Q0]), "depth" : 65 * mm});
        }
        {
            var Q0;
            Q0=qCreatedBy(makeId("Top.planeOp"),FACE);
            var sketch = newSketch(context, id + "F47", { "sketchPlane" : qUnion([Q0])});
            skLineSegment(sketch, "E105", {"start": v(420, 16.29) * mm, "end": v(420, -83.71) * mm, "construction": true});
            skSolve(sketch);
        }
        {
            var Q0;
            Q0=qCreatedBy(makeId("Top.planeOp"),FACE);
            var sketch = newSketch(context, id + "F48", { "sketchPlane" : qUnion([Q0])});
            skLineSegment(sketch, "E106", {"start": v(420, 0) * mm, "end": v(454.2, 0) * mm});
            skLineSegment(sketch, "E107", {"start": v(454.2, 0) * mm, "end": v(454.2, -30) * mm});
            skLineSegment(sketch, "E108", {"start": v(454.2, -30) * mm, "end": v(450.2, -30) * mm});
            skArc(sketch, "E109", {"start": v(420, -64) * mm, "mid": v(426.29, -57.36) * mm, "end": v(430, -49) * mm});
            skArc(sketch, "E110", {"start": v(445, -57.5) * mm, "mid": v(437.87, -52.6) * mm, "end": v(430, -49) * mm});
            skArc(sketch, "E111", {"start": v(449.53, -59.5) * mm, "mid": v(453.03, -63) * mm, "end": v(456.53, -59.5) * mm});
            skLineSegment(sketch, "E112", {"start": v(445, -57.5) * mm, "end": v(449.53, -59.5) * mm});
            skLineSegment(sketch, "E113", {"start": v(456.53, -59.5) * mm, "end": v(458.03, -59.5) * mm});
            skLineSegment(sketch, "E114", {"start": v(458.03, -59.5) * mm, "end": v(458.03, -59) * mm});
            skLineSegment(sketch, "E115", {"start": v(458.03, -59) * mm, "end": v(458.53, -59) * mm});
            skLineSegment(sketch, "E116", {"start": v(458.53, -59) * mm, "end": v(458.53, -59.5) * mm});
            skLineSegment(sketch, "E117", {"start": v(458.53, -59.5) * mm, "end": v(466.53, -59.5) * mm});
            skPoint(sketch, "E117.endSnap0", {"position": v(457.28, -59.5) * mm});
            skLineSegment(sketch, "E118", {"start": v(420, -67.5) * mm, "end": v(470, -67.5) * mm});
            skLineSegment(sketch, "E119", {"start": v(470, -67.5) * mm, "end": v(470, 2.5) * mm});
            skLineSegment(sketch, "E120", {"start": v(470, 2.5) * mm, "end": v(420, 2.5) * mm});
            skLineSegment(sketch, "E121", {"start": v(420, 2.5) * mm, "end": v(420, 0) * mm});
            skLineSegment(sketch, "E122", {"start": v(466.53, -56.5) * mm, "end": v(456.53, -56.5) * mm});
            skLineSegment(sketch, "E123", {"start": v(420, -67.5) * mm, "end": v(420, -64) * mm});
            skLineSegment(sketch, "E124", {"start": v(466.53, -59.5) * mm, "end": v(466.53, -56.5) * mm});
            skArc(sketch, "E125", {"start": v(453.12, -32.3) * mm, "mid": v(452.06, -30.65) * mm, "end": v(450.2, -30) * mm});
            skLineSegment(sketch, "E126", {"start": v(453.12, -32.3) * mm, "end": v(456.53, -56.5) * mm});
            skSolve(sketch);
        }
        {
            var Q0;
            Q0 = qSketchRegion(id + "F48", true);
            var Q1;
            Q1=sQuery(id+"F47.wireOp",EDGE,"E105");
            revolve(context, id + "F49", {"operationType" : NewBodyOperationType.REMOVE, "entities" : qUnion([Q0]), "axis" : qUnion([Q1]), "revolveType" : RevolveType.FULL, "oppositeDirection" : true});
        }
        {
            var Q0;
            Q0=makeQuery(id+"F49.boolean.opBoolean","COPY",FACE,{"derivedFrom":makeQuery(id+"F49.opRevolve","SWEPT_FACE",FACE,{"disambiguationData":[OSD([sQuery(id+"F48.wireOp",EDGE,"E117")])]})});
            var sketch = newSketch(context, id + "F50", { "sketchPlane" : qUnion([Q0])});
            skLineSegment(sketch, "E127.bottom", {"start": v(390.12, -29.88) * mm, "end": v(449.88, -29.88) * mm, "construction": true});
            skLineSegment(sketch, "E127.top", {"start": v(390.12, 29.88) * mm, "end": v(449.88, 29.88) * mm, "construction": true});
            skLineSegment(sketch, "E127.left", {"start": v(390.12, -29.88) * mm, "end": v(390.12, 29.88) * mm, "construction": true});
            skLineSegment(sketch, "E127.right", {"start": v(449.88, -29.88) * mm, "end": v(449.88, 29.88) * mm, "construction": true});
            skPoint(sketch, "E127.middle", {"position": v(420, 0) * mm});
            skCircle(sketch, "E128", {"center": v(390.12, 29.88) * mm, "radius": 2.5 * mm});
            skCircle(sketch, "E129", {"center": v(449.88, 29.88) * mm, "radius": 2.5 * mm});
            skCircle(sketch, "E130", {"center": v(449.88, -29.88) * mm, "radius": 2.5 * mm});
            skCircle(sketch, "E131", {"center": v(390.12, -29.88) * mm, "radius": 2.5 * mm});
            skSolve(sketch);
        }
        {
            var Q0;
            Q0 = qSketchRegion(id + "F50", true);
            extrude(context, id + "F51", {"entities" : qUnion([Q0]), "operationType" : NewBodyOperationType.REMOVE, "oppositeDirection" : true, "depth" : 5 * mm});
        }
        {
            var Q0;
            Q0=makeQuery(id+"F49.boolean.opBoolean","COPY",EDGE,{"derivedFrom":makeQuery(id+"F49.opRevolve","SWEPT_EDGE",EDGE,{"disambiguationData":[OSD([sQuery(id+"F48.wireOp",EDGE,"E106"),sQuery(id+"F48.wireOp",EDGE,"E107")])]})});
            var Q1;
            Q1=makeQuery(id+"F49.boolean.opBoolean","COPY",EDGE,{"derivedFrom":makeQuery(id+"F49.opRevolve","SWEPT_EDGE",EDGE,{"disambiguationData":[OSD([sQuery(id+"F48.wireOp",EDGE,"E107"),sQuery(id+"F48.wireOp",EDGE,"E108")])]})});
            fillet(context, id + "F52", {"entities" : qUnion([Q0, Q1]), "radius" : 2 * mm, "tangentPropagation" : true, "allowEdgeOverflow" : false});
        }
        {
            var Q0;
            Q0=qCreatedBy(makeId("Top.planeOp"),FACE);
            var sketch = newSketch(context, id + "F53", { "sketchPlane" : qUnion([Q0])});
            skLineSegment(sketch, "E132.bottom", {"start": v(-300, -110) * mm, "end": v(-408, -110) * mm});
            skLineSegment(sketch, "E132.top", {"start": v(-300, -106) * mm, "end": v(-408, -106) * mm});
            skLineSegment(sketch, "E132.left", {"start": v(-300, -110) * mm, "end": v(-300, -106) * mm});
            skLineSegment(sketch, "E132.right", {"start": v(-408, -110) * mm, "end": v(-408, -106) * mm});
            skSolve(sketch);
        }
        {
            var Q0;
            Q0 = qSketchRegion(id + "F53", true);
            extrude(context, id + "F54", {"entities" : qUnion([Q0]), "depth" : 240 * mm});
        }
        {
            var Q0;
            Q0=makeQuery(id+"F54.opExtrude","SWEPT_FACE",FACE,{"disambiguationData":[OSD([sQuery(id+"F53.wireOp",EDGE,"E132.bottom")])]});
            var sketch = newSketch(context, id + "F55", { "sketchPlane" : qUnion([Q0])});
            skCircle(sketch, "E133", {"center": v(-354, 185) * mm, "radius": 39 * mm});
            skPoint(sketch, "E133.centerSnap0", {"position": v(-354, 240) * mm});
            skSolve(sketch);
        }
        {
            var Q0;
            Q0 = qSketchRegion(id + "F55", true);
            extrude(context, id + "F56", {"entities" : qUnion([Q0]), "operationType" : NewBodyOperationType.REMOVE, "oppositeDirection" : true, "depth" : 5 * mm});
        }
        {
            var Q0;
            Q0=qCreatedBy(makeId("Top.planeOp"),FACE);
            var sketch = newSketch(context, id + "F57", { "sketchPlane" : qUnion([Q0])});
            skLineSegment(sketch, "E134.bottom", {"start": v(-569.47, -110) * mm, "end": v(-461.47, -110) * mm});
            skLineSegment(sketch, "E134.top", {"start": v(-569.47, -100) * mm, "end": v(-461.47, -100) * mm});
            skLineSegment(sketch, "E134.left", {"start": v(-569.47, -110) * mm, "end": v(-569.47, -100) * mm});
            skLineSegment(sketch, "E134.right", {"start": v(-461.47, -110) * mm, "end": v(-461.47, -100) * mm});
            skPoint(sketch, "E134.middle", {"position": v(-515.47, -105) * mm});
            skSolve(sketch);
        }
        {
            var Q0;
            Q0 = qSketchRegion(id + "F57", true);
            extrude(context, id + "F58", {"entities" : qUnion([Q0]), "depth" : 240 * mm, "offsetDistance" : 25 * mm});
        }
        {
            var Q0;
            Q0=makeQuery(id+"F58.opExtrude","SWEPT_FACE",FACE,{"disambiguationData":[OSD([sQuery(id+"F57.wireOp",EDGE,"E134.bottom")])]});
            var sketch = newSketch(context, id + "F59", { "sketchPlane" : qUnion([Q0])});
            skCircle(sketch, "E135", {"center": v(-515.47, 185) * mm, "radius": 47 * mm});
            skPoint(sketch, "E135.centerSnap0", {"position": v(-515.47, 240) * mm});
            skSolve(sketch);
        }
        {
            var Q0;
            Q0 = qSketchRegion(id + "F59", true);
            extrude(context, id + "F60", {"entities" : qUnion([Q0]), "operationType" : NewBodyOperationType.REMOVE, "oppositeDirection" : true, "depth" : 4 * mm, "offsetDistance" : 25 * mm});
        }
        {
            var Q0;
            Q0=makeQuery(id+"F60.boolean.opBoolean","COPY",FACE,{"derivedFrom":makeQuery(id+"F60.opExtrude","CAP_FACE",FACE,{"disambiguationData":[OSD([sQuery(id+"F59.wireOp",EDGE,"E135")])],"isStart":false})});
            var sketch = newSketch(context, id + "F61", { "sketchPlane" : qUnion([Q0])});
            skCircle(sketch, "E136", {"center": v(-515.47, 185) * mm, "radius": 36 * mm});
            skSolve(sketch);
        }
        {
            var Q0;
            Q0 = qSketchRegion(id + "F61", true);
            extrude(context, id + "F62", {"entities" : qUnion([Q0]), "operationType" : NewBodyOperationType.REMOVE, "oppositeDirection" : true, "depth" : 10 * mm, "offsetDistance" : 25 * mm});
        }
        {
            var Q0;
            Q0=qCreatedBy(makeId("Top.planeOp"),FACE);
            var sketch = newSketch(context, id + "F63", { "sketchPlane" : qUnion([Q0])});
            skLineSegment(sketch, "E137.bottom", {"start": v(-749.5, 100) * mm, "end": v(-641.5, 100) * mm});
            skLineSegment(sketch, "E137.top", {"start": v(-749.5, 110) * mm, "end": v(-641.5, 110) * mm});
            skLineSegment(sketch, "E137.left", {"start": v(-749.5, 100) * mm, "end": v(-749.5, 110) * mm});
            skLineSegment(sketch, "E137.right", {"start": v(-641.5, 100) * mm, "end": v(-641.5, 110) * mm});
            skPoint(sketch, "E137.middle", {"position": v(-695.5, 105) * mm});
            skSolve(sketch);
        }
        {
            var Q0;
            Q0 = qSketchRegion(id + "F63", true);
            extrude(context, id + "F64", {"entities" : qUnion([Q0]), "depth" : 230 * mm, "offsetDistance" : 25 * mm});
        }
        {
            var Q0;
            Q0=qCreatedBy(makeId("Top.planeOp"),FACE);
            var sketch = newSketch(context, id + "F65", { "sketchPlane" : qUnion([Q0])});
            skLineSegment(sketch, "E138.bottom", {"start": v(-920.07, -110) * mm, "end": v(-812.07, -110) * mm});
            skLineSegment(sketch, "E138.top", {"start": v(-920.07, 110) * mm, "end": v(-812.07, 110) * mm});
            skLineSegment(sketch, "E138.left", {"start": v(-920.07, -110) * mm, "end": v(-920.07, 110) * mm});
            skLineSegment(sketch, "E138.right", {"start": v(-812.07, -110) * mm, "end": v(-812.07, 110) * mm});
            skPoint(sketch, "E138.middle", {"position": v(-866.07, 0) * mm});
            skSolve(sketch);
        }
        {
            var Q0;
            Q0 = qSketchRegion(id + "F65", true);
            extrude(context, id + "F66", {"entities" : qUnion([Q0]), "depth" : 240 * mm, "offsetDistance" : 25 * mm});
        }
        {
            var Q0;
            Q0=makeQuery(id+"F66.opExtrude","SWEPT_FACE",FACE,{"disambiguationData":[OSD([sQuery(id+"F65.wireOp",EDGE,"E138.left")])]});
            var sketch = newSketch(context, id + "F67", { "sketchPlane" : qUnion([Q0])});
            skLineSegment(sketch, "E139", {"start": v(110, 240) * mm, "end": v(110, 0) * mm});
            skLineSegment(sketch, "E140", {"start": v(110, 0) * mm, "end": v(-110, 0) * mm});
            skLineSegment(sketch, "E141", {"start": v(110, 240) * mm, "end": v(-75, 240) * mm});
            skLineSegment(sketch, "E142", {"start": v(-76, 206) * mm, "end": v(-76, 90) * mm});
            skLineSegment(sketch, "E143", {"start": v(-66, 206) * mm, "end": v(-66, 90) * mm});
            skArc(sketch, "E144", {"start": v(-60, 206) * mm, "mid": v(-63.31, 224.85) * mm, "end": v(-75, 240) * mm});
            skLineSegment(sketch, "E145", {"start": v(-110, 240) * mm, "end": v(-110, 0) * mm});
            skArc(sketch, "E146", {"start": v(-82, 206) * mm, "mid": v(-87.27, 218.73) * mm, "end": v(-100, 224) * mm});
            skLineSegment(sketch, "E147", {"start": v(-100, 224) * mm, "end": v(-100, 230) * mm});
            skArc(sketch, "E148", {"start": v(-76, 206) * mm, "mid": v(-83.03, 222.97) * mm, "end": v(-100, 230) * mm});
            skLineSegment(sketch, "E149", {"start": v(-110, 240) * mm, "end": v(-100, 240) * mm});
            skArc(sketch, "E150", {"start": v(-66, 206) * mm, "mid": v(-75.96, 230.04) * mm, "end": v(-100, 240) * mm});
            skLineSegment(sketch, "E151", {"start": v(-82, 206) * mm, "end": v(-82, 90) * mm});
            skArc(sketch, "E152", {"start": v(-60, 90) * mm, "mid": v(0, 30) * mm, "end": v(60, 90) * mm});
            skPoint(sketch, "E152.centerSnap0", {"position": v(0, 0) * mm});
            skLineSegment(sketch, "E153", {"start": v(-60, 206) * mm, "end": v(-60, 90) * mm});
            skArc(sketch, "E154", {"start": v(-66, 90) * mm, "mid": v(0, 24) * mm, "end": v(66, 90) * mm});
            skArc(sketch, "E155", {"start": v(-76, 90) * mm, "mid": v(0, 14) * mm, "end": v(76, 90) * mm});
            skArc(sketch, "E156", {"start": v(-82, 90) * mm, "mid": v(0, 8) * mm, "end": v(82, 90) * mm});
            skArc(sketch, "E157", {"start": v(66, 90) * mm, "mid": v(63, 93) * mm, "end": v(60, 90) * mm});
            skArc(sketch, "E158", {"start": v(82, 90) * mm, "mid": v(79, 93) * mm, "end": v(76, 90) * mm});
            skSolve(sketch);
        }
        {
            var Q0;
            Q0 = qSketchRegion(id + "F67", true);
            extrude(context, id + "F68", {"entities" : qUnion([Q0]), "operationType" : NewBodyOperationType.REMOVE, "oppositeDirection" : true, "depth" : 110 * mm, "offsetDistance" : 25 * mm});
        }
        {
            var Q0;
            Q0=makeQuery(id+"F64.opExtrude","SWEPT_FACE",FACE,{"disambiguationData":[OSD([sQuery(id+"F63.wireOp",EDGE,"E137.left")])]});
            var sketch = newSketch(context, id + "F69", { "sketchPlane" : qUnion([Q0])});
            skArc(sketch, "E159", {"start": v(-100, 230) * mm, "mid": v(-105.48, 228.47) * mm, "end": v(-110, 225) * mm});
            skLineSegment(sketch, "E160", {"start": v(-110, 225) * mm, "end": v(-110, 230) * mm});
            skLineSegment(sketch, "E161", {"start": v(-110, 230) * mm, "end": v(-100, 230) * mm});
            skSolve(sketch);
        }
        {
            var Q0;
            Q0 = qSketchRegion(id + "F69", true);
            extrude(context, id + "F70", {"entities" : qUnion([Q0]), "operationType" : NewBodyOperationType.REMOVE, "oppositeDirection" : true, "depth" : 110 * mm, "offsetDistance" : 25 * mm});
        }
        {
            var Q0;
            Q0=makeQuery(id+"F34.boolean.opBoolean","COPY",FACE,{"derivedFrom":makeQuery(id+"F34.opExtrude","CAP_FACE",FACE,{"disambiguationData":[OSD([sQuery(id+"F33.wireOp",EDGE,"E74")])],"isStart":false})});
            var sketch = newSketch(context, id + "F71", { "sketchPlane" : qUnion([Q0])});
            skPoint(sketch, "E162.middle", {"position": v(-200, 185) * mm});
            skLineSegment(sketch, "E163.bottom", {"start": v(-229.88, 214.88) * mm, "end": v(-170.12, 214.88) * mm, "construction": true});
            skLineSegment(sketch, "E163.top", {"start": v(-229.88, 155.12) * mm, "end": v(-170.12, 155.12) * mm, "construction": true});
            skLineSegment(sketch, "E163.left", {"start": v(-229.88, 214.88) * mm, "end": v(-229.88, 155.12) * mm, "construction": true});
            skLineSegment(sketch, "E163.right", {"start": v(-170.12, 214.88) * mm, "end": v(-170.12, 155.12) * mm, "construction": true});
            skCircle(sketch, "E164", {"center": v(-229.88, 214.88) * mm, "radius": 2.5 * mm});
            skCircle(sketch, "E165", {"center": v(-170.12, 214.88) * mm, "radius": 2.5 * mm});
            skCircle(sketch, "E166", {"center": v(-229.88, 155.12) * mm, "radius": 2.5 * mm});
            skCircle(sketch, "E167", {"center": v(-170.12, 155.12) * mm, "radius": 2.5 * mm});
            skSolve(sketch);
        }
        {
            var Q0;
            Q0 = qSketchRegion(id + "F71", true);
            extrude(context, id + "F72", {"entities" : qUnion([Q0]), "operationType" : NewBodyOperationType.REMOVE, "oppositeDirection" : true, "depth" : 10 * mm, "offsetDistance" : 25 * mm});
        }
        {
            var Q0;
            Q0=makeQuery(id+"F26.boolean.opBoolean","COPY",FACE,{"derivedFrom":makeQuery(id+"F26.opExtrude","CAP_FACE",FACE,{"disambiguationData":[OSD([sQuery(id+"F25.wireOp",EDGE,"E40")])],"isStart":false})});
            var sketch = newSketch(context, id + "F73", { "sketchPlane" : qUnion([Q0])});
            skPoint(sketch, "E168.middle", {"position": v(0, 105) * mm});
            skLineSegment(sketch, "E169.bottom", {"start": v(-51.27, 156.27) * mm, "end": v(51.27, 156.27) * mm, "construction": true});
            skLineSegment(sketch, "E169.top", {"start": v(-51.27, 53.73) * mm, "end": v(51.27, 53.73) * mm, "construction": true});
            skLineSegment(sketch, "E169.left", {"start": v(-51.27, 156.27) * mm, "end": v(-51.27, 53.73) * mm, "construction": true});
            skLineSegment(sketch, "E169.right", {"start": v(51.27, 156.27) * mm, "end": v(51.27, 53.73) * mm, "construction": true});
            skCircle(sketch, "E170", {"center": v(-51.27, 156.27) * mm, "radius": 2.5 * mm});
            skCircle(sketch, "E171", {"center": v(51.27, 156.27) * mm, "radius": 2.5 * mm});
            skCircle(sketch, "E172", {"center": v(51.27, 53.73) * mm, "radius": 2.5 * mm});
            skCircle(sketch, "E173", {"center": v(-51.27, 53.73) * mm, "radius": 2.5 * mm});
            skSolve(sketch);
        }
        {
            var Q0;
            Q0 = qSketchRegion(id + "F73", true);
            extrude(context, id + "F74", {"entities" : qUnion([Q0]), "operationType" : NewBodyOperationType.REMOVE, "oppositeDirection" : true, "depth" : 15 * mm, "offsetDistance" : 25 * mm});
        }
        {
            var Q0;
            Q0=qCreatedBy(makeId("Front.planeOp"),FACE);
            var sketch = newSketch(context, id + "F75", { "sketchPlane" : qUnion([Q0])});
            skLineSegment(sketch, "E174", {"start": v(140, 23.5) * mm, "end": v(140, -16.5) * mm, "construction": true});
            skSolve(sketch);
        }
        {
            var Q0;
            Q0=qCreatedBy(makeId("Front.planeOp"),FACE);
            var sketch = newSketch(context, id + "F76", { "sketchPlane" : qUnion([Q0])});
            skLineSegment(sketch, "E175", {"start": v(140, 0) * mm, "end": v(141.9, 0) * mm});
            skLineSegment(sketch, "E176", {"start": v(141.9, 0) * mm, "end": v(141.9, 10) * mm});
            skLineSegment(sketch, "E177", {"start": v(141.9, 10) * mm, "end": v(143.5, 10) * mm});
            skLineSegment(sketch, "E178", {"start": v(140, 0) * mm, "end": v(140, 12) * mm});
            skLineSegment(sketch, "E179", {"start": v(140, 12) * mm, "end": v(141.5, 12) * mm});
            skArc(sketch, "E180", {"start": v(143.5, 10) * mm, "mid": v(142.71, 11.21) * mm, "end": v(141.5, 12) * mm});
            skSolve(sketch);
        }
        {
            var Q0;
            Q0 = qSketchRegion(id + "F76", true);
            var Q1;
            Q1=sQuery(id+"F75.wireOp",EDGE,"E174");
            revolve(context, id + "F77", {"surfaceOperationType" : NewSurfaceOperationType.NEW, "entities" : qUnion([Q0]), "axis" : qUnion([Q1]), "revolveType" : RevolveType.FULL});
        }
        {
            var Q0;
            Q0=makeQuery(id+"F77.opRevolve","SWEPT_FACE",FACE,{"disambiguationData":[OSD([sQuery(id+"F76.wireOp",EDGE,"E179")])]});
            var sketch = newSketch(context, id + "F78", { "sketchPlane" : qUnion([Q0])});
            skCircle(sketch, "E181.cCircle", {"center": v(140, 0) * mm, "radius": 1.44 * mm, "construction": true});
            skLineSegment(sketch, "E181.0", {"start": v(138.75, -0.72) * mm, "end": v(138.75, 0.72) * mm});
            skLineSegment(sketch, "E181.1", {"start": v(138.75, 0.72) * mm, "end": v(140, 1.44) * mm});
            skLineSegment(sketch, "E181.2", {"start": v(140, 1.44) * mm, "end": v(141.25, 0.72) * mm});
            skLineSegment(sketch, "E181.3", {"start": v(141.25, 0.72) * mm, "end": v(141.25, -0.72) * mm});
            skLineSegment(sketch, "E181.4", {"start": v(141.25, -0.72) * mm, "end": v(140, -1.44) * mm});
            skLineSegment(sketch, "E181.5", {"start": v(140, -1.44) * mm, "end": v(138.75, -0.72) * mm});
            skSolve(sketch);
        }
        {
            var Q0;
            Q0 = qSketchRegion(id + "F78", true);
            extrude(context, id + "F79", {"entities" : qUnion([Q0]), "operationType" : NewBodyOperationType.REMOVE, "oppositeDirection" : true, "depth" : 2 * mm, "offsetDistance" : 25 * mm});
        }
    });
